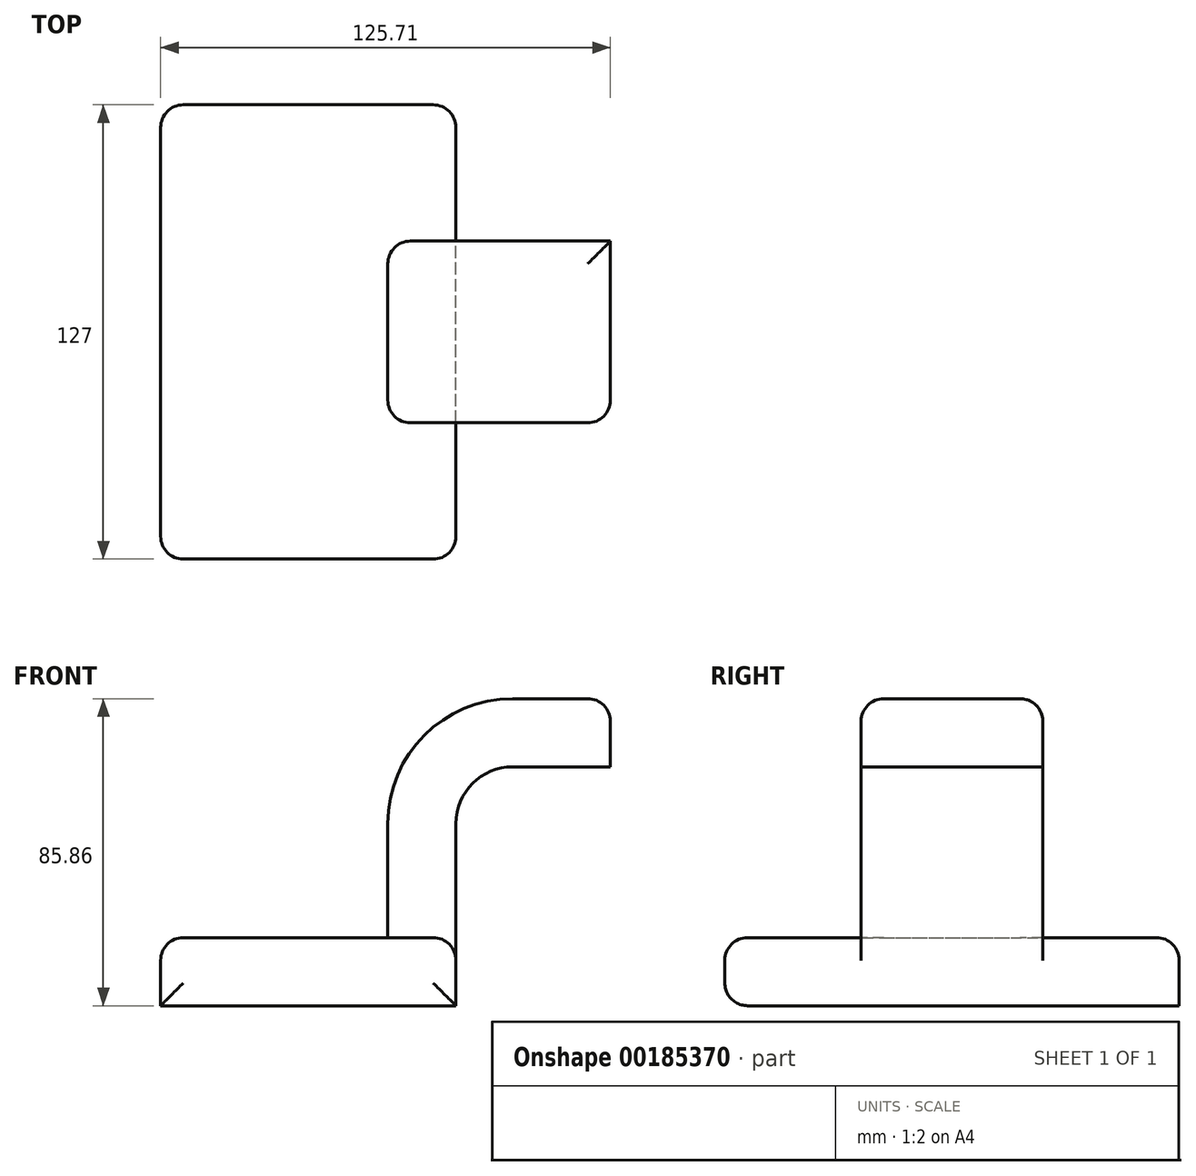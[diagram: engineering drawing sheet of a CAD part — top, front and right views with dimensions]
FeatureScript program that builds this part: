
annotation { "Feature Type Name" : "Feature", "Feature Type Description" : "" }
export const myFeature = defineFeature(function(context is Context, id is Id, definition is map)
    precondition{}
    {
        {
            var Q0;
            Q0=qCreatedBy(makeId("Front.planeOp"),FACE);
            var sketch = newSketch(context, id + "F0", { "sketchPlane" : qUnion([Q0])});
            skLineSegment(sketch, "E0.bottom", {"start": v(-41.28, 9.52) * mm, "end": v(41.27, 9.53) * mm});
            skLineSegment(sketch, "E0.top", {"start": v(-41.28, -9.53) * mm, "end": v(41.28, -9.53) * mm});
            skLineSegment(sketch, "E0.left", {"start": v(-41.28, 9.52) * mm, "end": v(-41.27, -9.53) * mm});
            skLineSegment(sketch, "E0.right", {"start": v(41.28, 9.53) * mm, "end": v(41.28, -9.52) * mm});
            skPoint(sketch, "E0.middle", {"position": v(0, 0) * mm});
            skLineSegment(sketch, "E1.bottom", {"start": v(96.82, 66.68) * mm, "end": v(59.04, 66.68) * mm});
            skLineSegment(sketch, "E1.top", {"start": v(109.84, 38.1) * mm, "end": v(59.04, 38.1) * mm});
            skLineSegment(sketch, "E1.left", {"start": v(109.84, 66.68) * mm, "end": v(109.84, 38.1) * mm});
            skLineSegment(sketch, "E1.right", {"start": v(59.04, 66.68) * mm, "end": v(59.04, 38.1) * mm});
            skPoint(sketch, "E1.middle", {"position": v(84.44, 52.39) * mm});
            skLineSegment(sketch, "E2", {"start": v(41.27, 9.53) * mm, "end": v(41.27, 41.4) * mm});
            skArc(sketch, "E3", {"start": v(41.27, 41.4) * mm, "mid": v(45.92, 52.63) * mm, "end": v(57.15, 57.28) * mm});
            skLineSegment(sketch, "E4", {"start": v(57.15, 57.28) * mm, "end": v(84.44, 57.28) * mm});
            skLineSegment(sketch, "E5.0", {"start": v(57.15, 76.33) * mm, "end": v(84.44, 76.33) * mm});
            skArc(sketch, "E5.1", {"start": v(22.23, 41.4) * mm, "mid": v(32.45, 66.1) * mm, "end": v(57.15, 76.33) * mm});
            skLineSegment(sketch, "E5.2", {"start": v(22.22, 9.53) * mm, "end": v(22.22, 41.4) * mm});
            skLineSegment(sketch, "E6", {"start": v(84.44, 57.28) * mm, "end": v(84.44, 76.33) * mm});
            skPoint(sketch, "E6.endSnap0", {"position": v(84.44, 66.68) * mm});
            skFitSpline(sketch, "E7", {"points": [v(-41.28, 9.52) * mm, v(57.15, 76.33) * mm], "startDerivative": vector(2.33, 104.26) * mm, "endDerivative": vector(134.07, -1.32) * mm});
            skFitSpline(sketch, "E8", {"points": [v(-41.28, 9.52) * mm, v(-41.28, 44.28) * mm], "startDerivative": vector(0, 22.27) * mm, "endDerivative": vector(0, 22.27) * mm});
            skSolve(sketch);
        }
        {
            var Q0;
            Q0=makeQuery(id+"F0.imprint","IMPRINT",FACE,{"disambiguationData":[TD([[makeQuery(id+"F0.imprint","IMPRINT",EDGE,{"derivedFrom":sQuery(id+"F0.wireOp",EDGE,"E0.top")}),1.0]])]});
            extrude(context, id + "F1", {"entities" : qUnion([Q0]), "endBound" : BoundingType.SYMMETRIC, "depth" : 127 * mm});
        }
        {
            var Q0;
            {var subQ0=sQuery(id+"F0.wireOp",EDGE,"E2");Q0=makeQuery(id+"F0.imprint","IMPRINT",FACE,{"disambiguationData":[TD([[makeQuery(id+"F0.imprint","IMPRINT",EDGE,{"derivedFrom":subQ0}),1.0]])]});}
            var Q1;
            {var subQ0=sQuery(id+"F0.wireOp",EDGE,"E1.right");var subQ1=sQuery(id+"F0.wireOp",EDGE,"E1.bottom");var subQ2=makeQuery(id+"F0.imprint","INTERSECT",VERTEX,{"derivedFrom":[subQ1,subQ0]});Q1=makeQuery(id+"F0.imprint","IMPRINT",FACE,{"disambiguationData":[TD([[makeQuery(id+"F0.imprint","IMPRINT",EDGE,{"disambiguationData":[TD([[subQ2,1.0]])],"derivedFrom":subQ1}),1.0]])]});}
            extrude(context, id + "F2", {"entities" : qUnion([Q0, Q1]), "operationType" : NewBodyOperationType.ADD, "endBound" : BoundingType.SYMMETRIC, "depth" : 50.8 * mm});
        }
        {
            var Q0;
            Q0=makeQuery(id+"F0.imprint","IMPRINT",FACE,{"disambiguationData":[TD([[makeQuery(id+"F0.imprint","IMPRINT",EDGE,{"derivedFrom":sQuery(id+"F0.wireOp",EDGE,"E5.1")}),1.0]])]});
            extrude(context, id + "F3", {"entities" : qUnion([Q0]), "operationType" : NewBodyOperationType.ADD, "endBound" : BoundingType.SYMMETRIC, "depth" : 16.5 * mm});
        }
        {
            var Q0;
            {var subQ0=sQuery(id+"F0.wireOp",EDGE,"E2");var subQ1=sQuery(id+"F0.wireOp",EDGE,"E0.bottom");var subQ2=sQuery(id+"F0.wireOp",EDGE,"E0.right");Q0=makeQuery(id+"F2.boolean.opBoolean","SPLIT",EDGE,{"disambiguationData":[TD([makeQuery(id+"F1.opExtrude","CAP_FACE",FACE,{"disambiguationData":[OSD([subQ1,sQuery(id+"F0.wireOp",EDGE,"E0.top"),sQuery(id+"F0.wireOp",EDGE,"E0.left"),subQ2])],"isStart":false})])],"derivedFrom":makeQuery(id+"F1.opExtrude","SWEPT_EDGE",EDGE,{"disambiguationData":[OSD([subQ1,subQ2,subQ0])]})});}
            var Q1;
            Q1=makeQuery(id+"F1.opExtrude","CAP_EDGE",EDGE,{"disambiguationData":[OSD([sQuery(id+"F0.wireOp",EDGE,"E0.right")])],"isStart":false});
            var Q2;
            {var subQ0=sQuery(id+"F0.wireOp",EDGE,"E2");var subQ1=sQuery(id+"F0.wireOp",EDGE,"E0.bottom");var subQ2=sQuery(id+"F0.wireOp",EDGE,"E0.right");Q2=makeQuery(id+"F2.boolean.opBoolean","SPLIT",EDGE,{"disambiguationData":[TD([makeQuery(id+"F1.opExtrude","CAP_FACE",FACE,{"disambiguationData":[OSD([subQ1,sQuery(id+"F0.wireOp",EDGE,"E0.top"),sQuery(id+"F0.wireOp",EDGE,"E0.left"),subQ2])],"isStart":true})])],"derivedFrom":makeQuery(id+"F1.opExtrude","SWEPT_EDGE",EDGE,{"disambiguationData":[OSD([subQ1,subQ2,subQ0])]})});}
            var Q3;
            Q3=makeQuery(id+"F1.opExtrude","CAP_EDGE",EDGE,{"disambiguationData":[OSD([sQuery(id+"F0.wireOp",EDGE,"E0.right")])],"isStart":true});
            var Q4;
            Q4=makeQuery(id+"F1.opExtrude","CAP_EDGE",EDGE,{"disambiguationData":[OSD([sQuery(id+"F0.wireOp",EDGE,"E0.bottom")])],"isStart":true});
            var Q5;
            Q5=makeQuery(id+"F1.opExtrude","CAP_EDGE",EDGE,{"disambiguationData":[OSD([sQuery(id+"F0.wireOp",EDGE,"E0.bottom")])],"isStart":false});
            var Q6;
            {var subQ0=sQuery(id+"F0.wireOp",EDGE,"E0.left");var subQ1=sQuery(id+"F0.wireOp",EDGE,"E0.bottom");var subQ2=sQuery(id+"F0.wireOp",EDGE,"E7");Q6=makeQuery(id+"F3.boolean.opBoolean","SPLIT",EDGE,{"disambiguationData":[TD([makeQuery(id+"F1.opExtrude","CAP_FACE",FACE,{"disambiguationData":[OSD([subQ1,sQuery(id+"F0.wireOp",EDGE,"E0.top"),subQ0,sQuery(id+"F0.wireOp",EDGE,"E0.right")])],"isStart":false})])],"derivedFrom":makeQuery(id+"F1.opExtrude","SWEPT_EDGE",EDGE,{"disambiguationData":[OSD([subQ1,subQ0,subQ2])]})});}
            var Q7;
            {var subQ0=sQuery(id+"F0.wireOp",EDGE,"E0.left");var subQ1=sQuery(id+"F0.wireOp",EDGE,"E7");var subQ2=sQuery(id+"F0.wireOp",EDGE,"E0.bottom");Q7=makeQuery(id+"F3.boolean.opBoolean","SPLIT",EDGE,{"disambiguationData":[TD([makeQuery(id+"F1.opExtrude","CAP_FACE",FACE,{"disambiguationData":[OSD([subQ2,sQuery(id+"F0.wireOp",EDGE,"E0.top"),subQ0,sQuery(id+"F0.wireOp",EDGE,"E0.right")])],"isStart":true})])],"derivedFrom":makeQuery(id+"F1.opExtrude","SWEPT_EDGE",EDGE,{"disambiguationData":[OSD([subQ2,subQ0,subQ1])]})});}
            var Q8;
            Q8=makeQuery(id+"F1.opExtrude","CAP_EDGE",EDGE,{"disambiguationData":[OSD([sQuery(id+"F0.wireOp",EDGE,"E0.top")])],"isStart":false});
            var Q9;
            Q9=makeQuery(id+"F1.opExtrude","CAP_EDGE",EDGE,{"disambiguationData":[OSD([sQuery(id+"F0.wireOp",EDGE,"E0.left")])],"isStart":false});
            var Q10;
            Q10=makeQuery(id+"F1.opExtrude","CAP_EDGE",EDGE,{"disambiguationData":[OSD([sQuery(id+"F0.wireOp",EDGE,"E0.left")])],"isStart":true});
            fillet(context, id + "F4", {"entities" : qUnion([Q0, Q1, Q2, Q3, Q4, Q5, Q6, Q7, Q8, Q9, Q10]), "radius" : 6.35 * mm, "tangentPropagation" : true, "allowEdgeOverflow" : false});
        }
        {
            var Q0;
            Q0=makeQuery(id+"F2.opExtrude","CAP_EDGE",EDGE,{"disambiguationData":[OSD([sQuery(id+"F0.wireOp",EDGE,"E6")])],"isStart":false});
            var Q1;
            Q1=makeQuery(id+"F2.opExtrude","CAP_EDGE",EDGE,{"disambiguationData":[OSD([sQuery(id+"F0.wireOp",EDGE,"E5.0")])],"isStart":false});
            var Q2;
            Q2=makeQuery(id+"F2.opExtrude","SWEPT_EDGE",EDGE,{"disambiguationData":[OSD([sQuery(id+"F0.wireOp",EDGE,"E5.0"),sQuery(id+"F0.wireOp",EDGE,"E6")])]});
            var Q3;
            Q3=makeQuery(id+"F2.opExtrude","CAP_EDGE",EDGE,{"disambiguationData":[OSD([sQuery(id+"F0.wireOp",EDGE,"E5.0")])],"isStart":true});
            fillet(context, id + "F5", {"entities" : qUnion([Q0, Q1, Q2, Q3]), "radius" : 6.35 * mm, "tangentPropagation" : true, "allowEdgeOverflow" : false});
        }
    });
